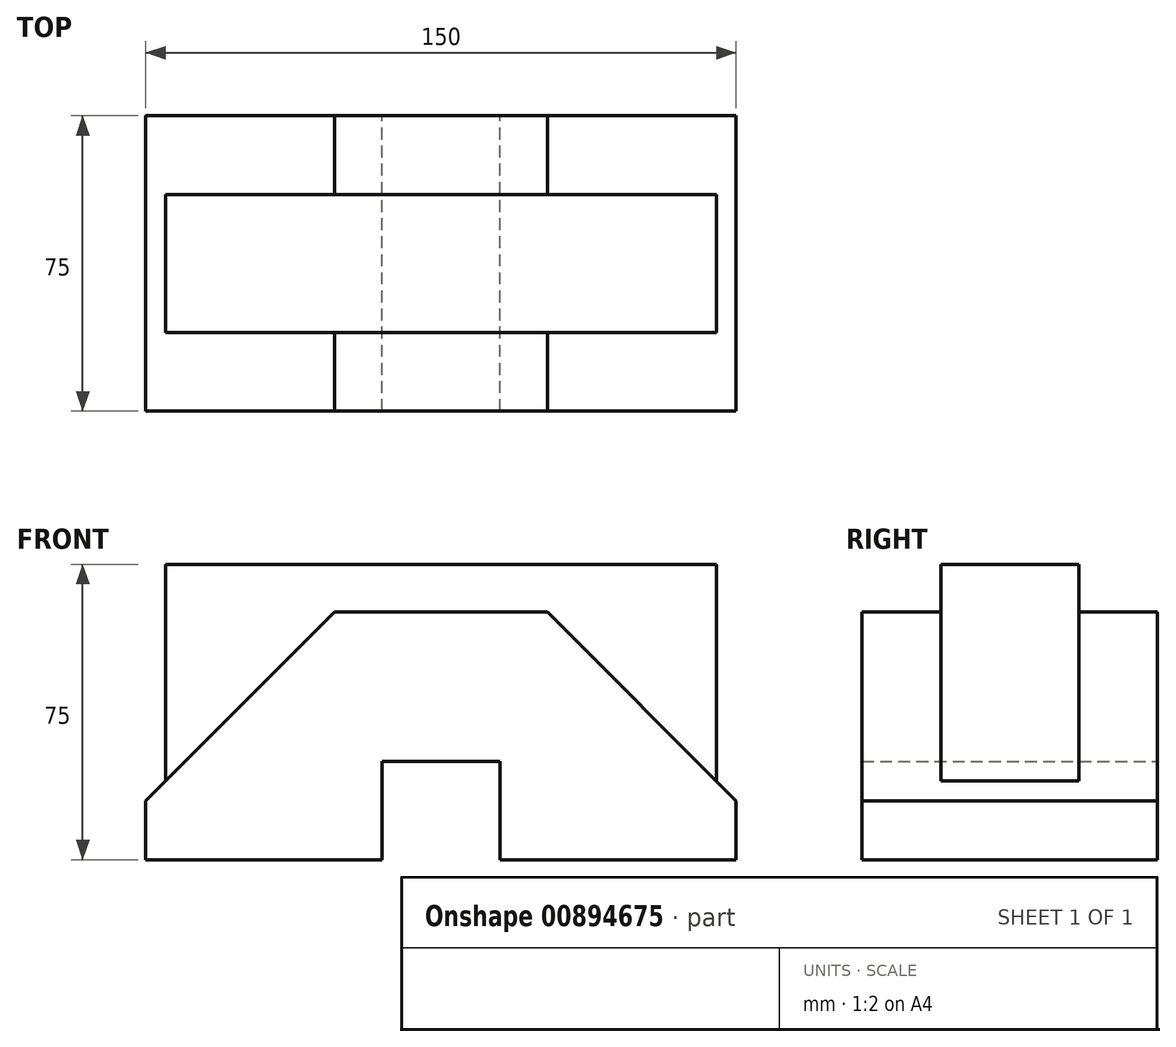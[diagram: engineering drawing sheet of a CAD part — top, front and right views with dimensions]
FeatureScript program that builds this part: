
annotation { "Feature Type Name" : "Feature", "Feature Type Description" : "" }
export const myFeature = defineFeature(function(context is Context, id is Id, definition is map)
    precondition{}
    {
        {
            var Q0;
            Q0=qCreatedBy(makeId("Front.planeOp"),FACE);
            var sketch = newSketch(context, id + "F0", { "sketchPlane" : qUnion([Q0])});
            skLineSegment(sketch, "E0.bottom", {"start": v(75, -37.5) * mm, "end": v(15, -37.5) * mm});
            skLineSegment(sketch, "E0.top", {"start": v(70, 37.5) * mm, "end": v(-70, 37.5) * mm});
            skLineSegment(sketch, "E0.left", {"start": v(75, -37.5) * mm, "end": v(75, -22.5) * mm});
            skPoint(sketch, "E0.middle", {"position": v(0, 0) * mm});
            skLineSegment(sketch, "E1.0", {"start": v(70, -17.5) * mm, "end": v(70, 37.5) * mm});
            skLineSegment(sketch, "E2.0", {"start": v(-70, -17.5) * mm, "end": v(-70, 37.5) * mm});
            skLineSegment(sketch, "E3.0", {"start": v(27, 25.5) * mm, "end": v(-27, 25.5) * mm});
            skPoint(sketch, "E4.orphan", {"position": v(75, 37.5) * mm});
            skPoint(sketch, "E5.orphan", {"position": v(-75, 37.5) * mm});
            skLineSegment(sketch, "E6", {"start": v(0, 35.13) * mm, "end": v(0, -43.77) * mm, "construction": true});
            skPoint(sketch, "E6.endSnap0", {"position": v(0, -37.5) * mm});
            skLineSegment(sketch, "E7", {"start": v(27, 25.5) * mm, "end": v(75, -22.5) * mm});
            skLineSegment(sketch, "E8.MirrorCS", {"start": v(-27, 25.5) * mm, "end": v(-75, -22.5) * mm});
            skLineSegment(sketch, "E9.0", {"start": v(15, -12.5) * mm, "end": v(15, -37.5) * mm});
            skLineSegment(sketch, "E10.MirrorCS", {"start": v(-15, -12.5) * mm, "end": v(-15, -37.5) * mm});
            skPoint(sketch, "E11.orphan", {"position": v(-15, 35.13) * mm});
            skPoint(sketch, "E12.orphan", {"position": v(15, 35.13) * mm});
            skPoint(sketch, "E13.orphan", {"position": v(15, -43.77) * mm});
            skPoint(sketch, "E14.orphan", {"position": v(-15, -43.77) * mm});
            skLineSegment(sketch, "E15.trimOffspring", {"start": v(15, -12.5) * mm, "end": v(-15, -12.5) * mm});
            skLineSegment(sketch, "E16.trimOffspring", {"start": v(-15, -37.5) * mm, "end": v(-75, -37.5) * mm});
            skLineSegment(sketch, "E17", {"start": v(-75, -22.5) * mm, "end": v(-75, -37.5) * mm});
            skSolve(sketch);
        }
        {
            var Q0;
            Q0=makeQuery(id+"F0.imprint","IMPRINT",FACE,{"disambiguationData":[TD([[makeQuery(id+"F0.imprint","IMPRINT",EDGE,{"derivedFrom":sQuery(id+"F0.wireOp",EDGE,"E0.bottom")}),-1.0]])]});
            var Q1;
            Q1=sQuery(id+"F0.wireOp",EDGE,"E7");
            var Q2;
            Q2=sQuery(id+"F0.wireOp",EDGE,"E3.0");
            var Q3;
            Q3=sQuery(id+"F0.wireOp",EDGE,"E8.MirrorCS");
            var Q4;
            Q4=sQuery(id+"F0.wireOp",EDGE,"E0.right");
            var Q5;
            Q5=sQuery(id+"F0.wireOp",EDGE,"E16.trimOffspring");
            extrude(context, id + "F1", {"entities" : qUnion([Q0]), "surfaceEntities" : qUnion([Q1, Q2, Q3, Q4, Q5]), "depth" : 75 * mm, "offsetDistance" : 25 * mm, "symmetric" : true});
        }
        {
            var Q0;
            Q0=makeQuery(id+"F0.imprint","IMPRINT",FACE,{"disambiguationData":[TD([[makeQuery(id+"F0.imprint","IMPRINT",EDGE,{"derivedFrom":sQuery(id+"F0.wireOp",EDGE,"E0.top")}),1.0]])]});
            extrude(context, id + "F2", {"entities" : qUnion([Q0]), "operationType" : NewBodyOperationType.ADD, "depth" : 35 * mm, "offsetDistance" : 25 * mm, "symmetric" : true});
        }
    });
